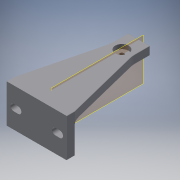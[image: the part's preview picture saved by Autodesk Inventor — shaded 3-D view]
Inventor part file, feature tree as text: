
AUTODESK INVENTOR PART (.ipt)
format: ipt  version: 2016 (Build 200138000, 138)  size: 429,568 bytes
history: native  units: mm
features: fillet x9, projected_geometry x9, extrude x8, sketch x7, chamfer x4, plane x1, pattern_linear x1
ambient origin geometry x8: Origin, YZ Plane, XZ Plane, XY Plane, X Axis, Y Axis, Z Axis, Center Point
bodies: Solid1 (feature_tree)
feature tree (39):
  extrude  "Extrusion1"  Depth=15.0mm
  extrude  "Extrusion7"  Depth=70.0mm
  extrude  "Extrusion8"  Depth=8.5mm
  extrude  "Extrusion9"  Depth=40.0mm TaperAngle=0.0deg
  chamfer  "Chamfer3"  Distance=35.0mm
  chamfer  "Chamfer4"  Distance=8.0mm
  plane  "Work Plane2"
  extrude  "Extrusion3"  Depth=8.0mm
  extrude  "Extrusion10"  Depth=10.0mm TaperAngle=0.0deg
  fillet  "Fillet3"  Radius=2.0mm
  fillet  "Fillet4"  Radius=6.8mm
  fillet  "Fillet5"  Radius=3.5mm
  fillet  "Fillet6"  Radius=20.0mm
  fillet  "Fillet7"  Radius=31.5mm
  fillet  "Fillet8"  Radius=10.0mm
  chamfer  "Chamfer5"  Distance=24.5mm
  fillet  "Fillet9"  Radius=8.0mm
  fillet  "Fillet10"  Radius=15.0mm
  fillet  "Fillet2"  Radius=140.0mm
  extrude  "Extrusion4"  Depth=140.0mm TaperAngle=45.0deg
  chamfer  "Chamfer1"  Distance=6.0mm
  extrude  "Extrusion6"  Depth=15.0mm TaperAngle=0.0deg
  pattern_linear  "Rectangular Pattern1"  Count1=4  [1 undecoded]
  sketch  "Sketch1"  dims[d1=172.0mm d2=15.0mm]
  projected_geometry  "Projected Loop1"
  sketch  "Sketch4"  dims[d3=15.0mm d4=70.0mm]
  projected_geometry  "Projected Loop3"
  sketch  "Sketch5"  dims[d5=40.0mm d6=0.0mm d7=8.5mm]
  projected_geometry  "Projected Loop4"
  sketch  "Sketch6"  dims[d31=-20.0mm d33=40.0mm d34=0.0mm]
  projected_geometry  "Projected Loop5"
  sketch  "Sketch7"  dims[d35=5.0mm]
  projected_geometry  "Projected Loop6"
  sketch  "Sketch8"  dims[d36=6.0mm]
  projected_geometry  "Projected Loop7"
  sketch  "Sketch9"  dims[d37=6.0mm d38=35.0mm d39=8.0mm d40=8.0mm d41=10.0mm d42=0.0mm d43=2.0mm d44=2.0mm d45=45.0deg d49=6.8mm d53=3.5mm d54=0.0mm d55=20.0mm d57=-12.0mm d58=20.0mm d60=-52.0mm d61=31.5mm d62=10.0mm d63=0.0mm d64=24.5mm d65=8.0mm d66=0.0mm d67=15.0mm d68=0.0mm d72=140.0mm d73=35.0mm d74=45.0deg d75=140.0mm d76=35.0mm d77=45.0deg d78=6.0mm d79=15.0mm d80=0.0mm d81=40.0mm d82=40.0mm d83=40.0mm d84=10.0mm d85=10.0mm d86=6.0mm d88=13.0mm d89=8.0mm d90=2.0mm d91=30.0mm d92=45.0deg d93=1.0mm d94=35.0mm d95=35.0mm d96=4.0mm]
  projected_geometry  "Projected Loop8"
  projected_geometry  "Project Cut Edges1"
  projected_geometry  "Project Cut Edges2"
note: 1 required parameter value undecoded (feature->parameter linkage not recoverable at this tier; creation-order binding heuristic only, values carry confidence <= 0.55)
